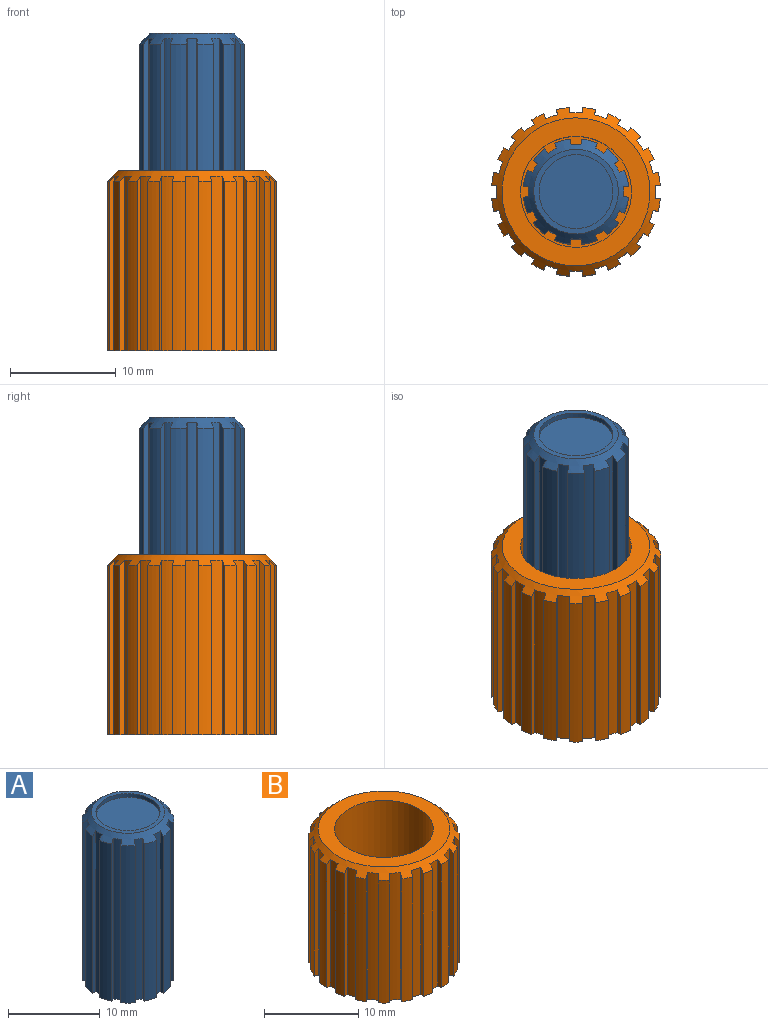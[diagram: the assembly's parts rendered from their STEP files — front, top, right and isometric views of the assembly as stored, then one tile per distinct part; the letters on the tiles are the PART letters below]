
ASSEMBLY  parts=2 mates=1
PART A: 59 faces, bbox 10x10x22 mm
  f0: cylinder r=5mm len=21mm, axis (0,0,-1), area 33mm2, adj f14,f18,f30,f53
  f1: cylinder r=5mm len=21mm, axis (0,0,-1), area 33mm2, adj f14,f18,f50,f54
  f2: cylinder r=5mm len=21mm, axis (0,0,-1), area 33mm2, adj f14,f18,f47,f51
  f3: cylinder r=5mm len=21mm, axis (0,0,-1), area 33mm2, adj f14,f18,f44,f48
  f4: cylinder r=5mm len=21mm, axis (0,0,-1), area 33mm2, adj f14,f18,f41,f45
  f5: cylinder r=5mm len=21mm, axis (0,0,-1), area 33mm2, adj f14,f18,f38,f42
  f6: cylinder r=5mm len=21mm, axis (0,0,-1), area 33mm2, adj f14,f18,f35,f39
  f7: cylinder r=5mm len=21mm, axis (0,0,-1), area 33mm2, adj f14,f18,f32,f36
  f8: cylinder r=5mm len=21mm, axis (0,0,-1), area 33mm2, adj f14,f18,f27,f29
  f9: cylinder r=5mm len=21mm, axis (0,0,-1), area 33mm2, adj f14,f18,f24,f26
  f10: cylinder r=5mm len=21mm, axis (0,0,-1), area 33mm2, adj f14,f18,f21,f23
  f11: plane 3.41x1mm, normal (0,0,-1), area 2.4mm2, adj f15,f16
  f12: cylinder r=5mm len=21mm, axis (0,0,-1), area 33mm2, adj f14,f18,f20,f33
  f13: plane 8x8mm, normal (0,0,1), area 11.8mm2, adj f18,f55
  f14: plane 9.95x9.95mm, normal (0,0,-1), area 60.6mm2, adj f0,f1,f2,f3,f4,f5,f6,f7
  f15: cylinder r=1.95mm len=8.7mm, axis (0,0,-1), area 83mm2, adj f11,f14,f16,f58
  f16: plane 5.7x3.41mm, normal (-1,0,0), area 19.4mm2, adj f11,f15,f57
  f17: plane 1.1x0.3mm, normal (0,0,-1), area 0.2mm2, adj f57,f58
  f18: cone r=4mm half-angle=45deg, axis (0,0,-1), area 31.5mm2, adj f0,f1,f2,f3,f4,f5,f6,f7
  f19: cylinder r=4.5mm len=21.5mm, axis (0,0,1), area 20.3mm2, adj f14,f18,f20,f21
  f20: plane 21.5x0.5mm, normal (-0.99,-0.1,0), area 10.6mm2, adj f12,f14,f18,f19
  f21: plane 21.5x0.5mm, normal (0.99,-0.1,0), area 10.6mm2, adj f10,f14,f18,f19
  f22: cylinder r=4.5mm len=21.5mm, axis (0,0,1), area 20.3mm2, adj f14,f18,f23,f24
  f23: plane 21.5x0.46mm, normal (-0.91,0.41,0), area 10.6mm2, adj f10,f14,f18,f22
  f24: plane 21.5x0.4mm, normal (0.81,-0.59,0), area 10.6mm2, adj f9,f14,f18,f22
  f25: cylinder r=4.5mm len=21.5mm, axis (0,0,1), area 20.3mm2, adj f14,f18,f26,f27
  f26: plane 21.5x0.4mm, normal (-0.59,0.81,0), area 10.6mm2, adj f9,f14,f18,f25
  f27: plane 21.5x0.46mm, normal (0.41,-0.91,0), area 10.6mm2, adj f8,f14,f18,f25
  f28: cylinder r=4.5mm len=21.5mm, axis (0,0,1), area 20.3mm2, adj f14,f18,f29,f30
  f29: plane 21.5x0.5mm, normal (-0.1,0.99,0), area 10.6mm2, adj f8,f14,f18,f28
  f30: plane 21.5x0.5mm, normal (-0.1,-0.99,0), area 10.6mm2, adj f0,f14,f18,f28
  f31: cylinder r=4.5mm len=21.5mm, axis (0,0,1), area 20.3mm2, adj f14,f18,f32,f33
  f32: plane 21.5x0.4mm, normal (-0.81,-0.59,0), area 10.6mm2, adj f7,f14,f18,f31
  f33: plane 21.5x0.46mm, normal (0.91,0.41,0), area 10.6mm2, adj f12,f14,f18,f31
  f34: cylinder r=4.5mm len=21.5mm, axis (0,0,1), area 20.3mm2, adj f14,f18,f35,f36
  f35: plane 21.5x0.46mm, normal (-0.41,-0.91,0), area 10.6mm2, adj f6,f14,f18,f34
  f36: plane 21.5x0.4mm, normal (0.59,0.81,0), area 10.6mm2, adj f7,f14,f18,f34
  f37: cylinder r=4.5mm len=21.5mm, axis (0,0,1), area 20.3mm2, adj f14,f18,f38,f39
  f38: plane 21.5x0.5mm, normal (0.1,-0.99,0), area 10.6mm2, adj f5,f14,f18,f37
  f39: plane 21.5x0.5mm, normal (0.1,0.99,0), area 10.6mm2, adj f6,f14,f18,f37
  f40: cylinder r=4.5mm len=21.5mm, axis (0,0,1), area 20.3mm2, adj f14,f18,f41,f42
  f41: plane 21.5x0.4mm, normal (0.59,-0.81,0), area 10.6mm2, adj f4,f14,f18,f40
  f42: plane 21.5x0.46mm, normal (-0.41,0.91,0), area 10.6mm2, adj f5,f14,f18,f40
  f43: cylinder r=4.5mm len=21.5mm, axis (0,0,1), area 20.3mm2, adj f14,f18,f44,f45
  f44: plane 21.5x0.46mm, normal (0.91,-0.41,0), area 10.6mm2, adj f3,f14,f18,f43
  f45: plane 21.5x0.4mm, normal (-0.81,0.59,0), area 10.6mm2, adj f4,f14,f18,f43
  f46: cylinder r=4.5mm len=21.5mm, axis (0,0,1), area 20.3mm2, adj f14,f18,f47,f48
  f47: plane 21.5x0.5mm, normal (0.99,0.1,0), area 10.6mm2, adj f2,f14,f18,f46
  f48: plane 21.5x0.5mm, normal (-0.99,0.1,0), area 10.6mm2, adj f3,f14,f18,f46
  f49: cylinder r=4.5mm len=21.5mm, axis (0,0,1), area 20.3mm2, adj f14,f18,f50,f51
  f50: plane 21.5x0.4mm, normal (0.81,0.59,0), area 10.6mm2, adj f1,f14,f18,f49
  f51: plane 21.5x0.46mm, normal (-0.91,-0.41,0), area 10.6mm2, adj f2,f14,f18,f49
  f52: cylinder r=4.5mm len=21.5mm, axis (0,0,1), area 20.3mm2, adj f14,f18,f53,f54
  f53: plane 21.5x0.46mm, normal (0.41,0.91,0), area 10.6mm2, adj f0,f14,f18,f52
  f54: plane 21.5x0.4mm, normal (-0.59,-0.81,0), area 10.6mm2, adj f1,f14,f18,f52
  f55: cylinder r=3.5mm len=7mm, axis (0,0,1), area 11mm2, adj f13,f56
  f56: plane 7x7mm, normal (0,0,1), area 38.5mm2, adj f55
  f57: plane 3.41x1.3mm, normal (-0.71,0,-0.71), area 4.5mm2, adj f16,f17,f58
  f58: cone r=0.65mm half-angle=45deg, axis (0,0,-1), area 8.6mm2, adj f15,f17,f57
PART B: 94 faces, bbox 16x16x17 mm
  f0: plane 4.5x0.43mm, normal (0,1,0), area 1.9mm2, adj f1,f26,f31,f93
  f1: plane 4.5x1.6mm, normal (1,0,0), area 7.2mm2, adj f0,f2,f26,f93
  f2: plane 4.5x0.43mm, normal (0,-1,0), area 1.9mm2, adj f1,f26,f31,f93
  f3: plane 4.5x0.43mm, normal (0,-1,0), area 1.9mm2, adj f4,f26,f31,f92
  f4: plane 4.5x1.6mm, normal (-1,0,0), area 7.2mm2, adj f3,f5,f26,f92
  f5: plane 4.5x0.43mm, normal (0,1,0), area 1.9mm2, adj f4,f26,f31,f92
  f6: cylinder r=8mm len=16mm, axis (0,0,-1), area 20.1mm2, adj f25,f29,f88,f89
  f7: cylinder r=8mm len=16mm, axis (0,0,-1), area 20.1mm2, adj f25,f29,f85,f86
  f8: cylinder r=8mm len=16mm, axis (0,0,-1), area 20.1mm2, adj f25,f29,f82,f83
  f9: cylinder r=8mm len=16mm, axis (0,0,-1), area 20.1mm2, adj f25,f29,f79,f80
  f10: cylinder r=8mm len=16mm, axis (0,0,-1), area 20.1mm2, adj f25,f29,f76,f77
  f11: cylinder r=8mm len=16mm, axis (0,0,-1), area 20.1mm2, adj f25,f29,f73,f74
  f12: cylinder r=8mm len=16mm, axis (0,0,-1), area 20.1mm2, adj f25,f29,f70,f71
  f13: cylinder r=8mm len=16mm, axis (0,0,-1), area 20.1mm2, adj f25,f29,f61,f68
  f14: cylinder r=8mm len=16mm, axis (0,0,-1), area 20.1mm2, adj f25,f29,f55,f65
  f15: cylinder r=8mm len=16mm, axis (0,0,-1), area 20.1mm2, adj f25,f29,f62,f67
  f16: cylinder r=8mm len=16mm, axis (0,0,-1), area 20.1mm2, adj f25,f29,f59,f64
  f17: cylinder r=8mm len=16mm, axis (0,0,-1), area 20.1mm2, adj f25,f29,f37,f56
  f18: cylinder r=8mm len=16mm, axis (0,0,-1), area 20.1mm2, adj f25,f29,f52,f53
  f19: cylinder r=8mm len=16mm, axis (0,0,-1), area 20.1mm2, adj f25,f29,f49,f50
  f20: cylinder r=8mm len=16mm, axis (0,0,-1), area 20.1mm2, adj f25,f29,f46,f47
  f21: cylinder r=8mm len=16mm, axis (0,0,-1), area 20.1mm2, adj f25,f29,f43,f44
  f22: cylinder r=8mm len=16mm, axis (0,0,-1), area 20.1mm2, adj f25,f29,f40,f41
  f23: cylinder r=8mm len=16mm, axis (0,0,-1), area 20.1mm2, adj f25,f29,f38,f58
  f24: cylinder r=8mm len=16mm, axis (0,0,-1), area 20.1mm2, adj f25,f29,f34,f35
  f25: cone r=7mm half-angle=45deg, axis (0,0,-1), area 49.4mm2, adj f6,f7,f8,f9,f10,f11,f12,f13
  f26: plane 10.5x10.5mm, normal (0,0,1), area 65.3mm2, adj f0,f1,f2,f3,f4,f5,f30,f31
  f27: cylinder r=8mm len=16mm, axis (0,0,-1), area 20.1mm2, adj f25,f29,f32,f91
  f28: plane 14x14mm, normal (0,0,1), area 67.3mm2, adj f25,f30
  f29: plane 15.95x15.95mm, normal (0,0,-1), area 166mm2, adj f6,f7,f8,f9,f10,f11,f12,f13
  f30: cylinder r=5.25mm len=10.5mm, axis (0,0,1), area 346.4mm2, adj f26,f28
  f31: cylinder r=2.7mm len=6.5mm, axis (0,0,1), area 95.7mm2, adj f0,f2,f3,f5,f26,f29,f92,f93
  f32: plane 16.5x0.46mm, normal (0.92,0.38,0), area 8.1mm2, adj f25,f27,f29,f33
  f33: cylinder r=7.5mm len=16.5mm, axis (0,0,1), area 19.4mm2, adj f25,f29,f32,f34
  f34: plane 16.5x0.49mm, normal (-0.97,-0.23,0), area 8.1mm2, adj f24,f25,f29,f33
  f35: plane 16.5x0.5mm, normal (1,0.08,0), area 8.1mm2, adj f24,f25,f29,f36
  f36: cylinder r=7.5mm len=16.5mm, axis (0,0,1), area 19.4mm2, adj f25,f29,f35,f37
  f37: plane 16.5x0.5mm, normal (-1,0.08,0), area 8.1mm2, adj f17,f25,f29,f36
  f38: plane 16.5x0.43mm, normal (0.85,-0.52,0), area 8.1mm2, adj f23,f25,f29,f39
  f39: cylinder r=7.5mm len=16.5mm, axis (0,0,1), area 19.4mm2, adj f25,f29,f38,f40
  f40: plane 16.5x0.38mm, normal (-0.76,0.65,0), area 8.1mm2, adj f22,f25,f29,f39
  f41: plane 16.5x0.38mm, normal (0.65,-0.76,0), area 8.1mm2, adj f22,f25,f29,f42
  f42: cylinder r=7.5mm len=16.5mm, axis (0,0,1), area 19.4mm2, adj f25,f29,f41,f43
  f43: plane 16.5x0.43mm, normal (-0.52,0.85,0), area 8.1mm2, adj f21,f25,f29,f42
  f44: plane 16.5x0.46mm, normal (0.38,-0.92,0), area 8.1mm2, adj f21,f25,f29,f45
  f45: cylinder r=7.5mm len=16.5mm, axis (0,0,1), area 19.4mm2, adj f25,f29,f44,f46
  f46: plane 16.5x0.49mm, normal (-0.23,0.97,0), area 8.1mm2, adj f20,f25,f29,f45
  f47: plane 16.5x0.5mm, normal (0.08,-1,0), area 8.1mm2, adj f20,f25,f29,f48
  f48: cylinder r=7.5mm len=16.5mm, axis (0,0,1), area 19.4mm2, adj f25,f29,f47,f49
  f49: plane 16.5x0.5mm, normal (0.08,1,0), area 8.1mm2, adj f19,f25,f29,f48
  f50: plane 16.5x0.49mm, normal (-0.23,-0.97,0), area 8.1mm2, adj f19,f25,f29,f51
  f51: cylinder r=7.5mm len=16.5mm, axis (0,0,1), area 19.4mm2, adj f25,f29,f50,f52
  f52: plane 16.5x0.46mm, normal (0.38,0.92,0), area 8.1mm2, adj f18,f25,f29,f51
  f53: plane 16.5x0.43mm, normal (-0.52,-0.85,0), area 8.1mm2, adj f18,f25,f29,f54
  f54: cylinder r=7.5mm len=16.5mm, axis (0,0,1), area 19.4mm2, adj f25,f29,f53,f55
  f55: plane 16.5x0.38mm, normal (0.65,0.76,0), area 8.1mm2, adj f14,f25,f29,f54
  f56: plane 16.5x0.49mm, normal (0.97,-0.23,0), area 8.1mm2, adj f17,f25,f29,f57
  f57: cylinder r=7.5mm len=16.5mm, axis (0,0,1), area 19.4mm2, adj f25,f29,f56,f58
  f58: plane 16.5x0.46mm, normal (-0.92,0.38,0), area 8.1mm2, adj f23,f25,f29,f57
  f59: plane 16.5x0.5mm, normal (-1,-0.08,0), area 8.1mm2, adj f16,f25,f29,f60
  f60: cylinder r=7.5mm len=16.5mm, axis (0,0,1), area 19.4mm2, adj f25,f29,f59,f61
  f61: plane 16.5x0.5mm, normal (1,-0.08,0), area 8.1mm2, adj f13,f25,f29,f60
  f62: plane 16.5x0.46mm, normal (-0.92,-0.38,0), area 8.1mm2, adj f15,f25,f29,f63
  f63: cylinder r=7.5mm len=16.5mm, axis (0,0,1), area 19.4mm2, adj f25,f29,f62,f64
  f64: plane 16.5x0.49mm, normal (0.97,0.23,0), area 8.1mm2, adj f16,f25,f29,f63
  f65: plane 16.5x0.38mm, normal (-0.76,-0.65,0), area 8.1mm2, adj f14,f25,f29,f66
  f66: cylinder r=7.5mm len=16.5mm, axis (0,0,1), area 19.4mm2, adj f25,f29,f65,f67
  f67: plane 16.5x0.43mm, normal (0.85,0.52,0), area 8.1mm2, adj f15,f25,f29,f66
  f68: plane 16.5x0.49mm, normal (-0.97,0.23,0), area 8.1mm2, adj f13,f25,f29,f69
  f69: cylinder r=7.5mm len=16.5mm, axis (0,0,1), area 19.4mm2, adj f25,f29,f68,f70
  f70: plane 16.5x0.46mm, normal (0.92,-0.38,0), area 8.1mm2, adj f12,f25,f29,f69
  f71: plane 16.5x0.43mm, normal (-0.85,0.52,0), area 8.1mm2, adj f12,f25,f29,f72
  f72: cylinder r=7.5mm len=16.5mm, axis (0,0,1), area 19.4mm2, adj f25,f29,f71,f73
  f73: plane 16.5x0.38mm, normal (0.76,-0.65,0), area 8.1mm2, adj f11,f25,f29,f72
  f74: plane 16.5x0.38mm, normal (-0.65,0.76,0), area 8.1mm2, adj f11,f25,f29,f75
  f75: cylinder r=7.5mm len=16.5mm, axis (0,0,1), area 19.4mm2, adj f25,f29,f74,f76
  f76: plane 16.5x0.43mm, normal (0.52,-0.85,0), area 8.1mm2, adj f10,f25,f29,f75
  f77: plane 16.5x0.46mm, normal (-0.38,0.92,0), area 8.1mm2, adj f10,f25,f29,f78
  f78: cylinder r=7.5mm len=16.5mm, axis (0,0,1), area 19.4mm2, adj f25,f29,f77,f79
  f79: plane 16.5x0.49mm, normal (0.23,-0.97,0), area 8.1mm2, adj f9,f25,f29,f78
  f80: plane 16.5x0.5mm, normal (-0.08,1,0), area 8.1mm2, adj f9,f25,f29,f81
  f81: cylinder r=7.5mm len=16.5mm, axis (0,0,1), area 19.4mm2, adj f25,f29,f80,f82
  f82: plane 16.5x0.5mm, normal (-0.08,-1,0), area 8.1mm2, adj f8,f25,f29,f81
  f83: plane 16.5x0.49mm, normal (0.23,0.97,0), area 8.1mm2, adj f8,f25,f29,f84
  f84: cylinder r=7.5mm len=16.5mm, axis (0,0,1), area 19.4mm2, adj f25,f29,f83,f85
  f85: plane 16.5x0.46mm, normal (-0.38,-0.92,0), area 8.1mm2, adj f7,f25,f29,f84
  f86: plane 16.5x0.43mm, normal (0.52,0.85,0), area 8.1mm2, adj f7,f25,f29,f87
  f87: cylinder r=7.5mm len=16.5mm, axis (0,0,1), area 19.4mm2, adj f25,f29,f86,f88
  f88: plane 16.5x0.38mm, normal (-0.65,-0.76,0), area 8.1mm2, adj f6,f25,f29,f87
  f89: plane 16.5x0.38mm, normal (0.76,0.65,0), area 8.1mm2, adj f6,f25,f29,f90
  f90: cylinder r=7.5mm len=16.5mm, axis (0,0,1), area 19.4mm2, adj f25,f29,f89,f91
  f91: plane 16.5x0.43mm, normal (-0.85,-0.52,0), area 8.1mm2, adj f25,f27,f29,f90
  f92: plane 1.6x0.55mm, normal (0,0,-1), area 0.8mm2, adj f3,f4,f5,f31
  f93: plane 1.6x0.55mm, normal (0,0,-1), area 0.8mm2, adj f0,f1,f2,f31
PLACE A t=(-15.92,-10.21,-1.53)mm
PLACE B t=(-15.92,-10.21,-3.03)mm
MATE revolute B.f31 <-> A.f15  axis (0,0,1) through (-15.92,-10.21,4.97)mm
